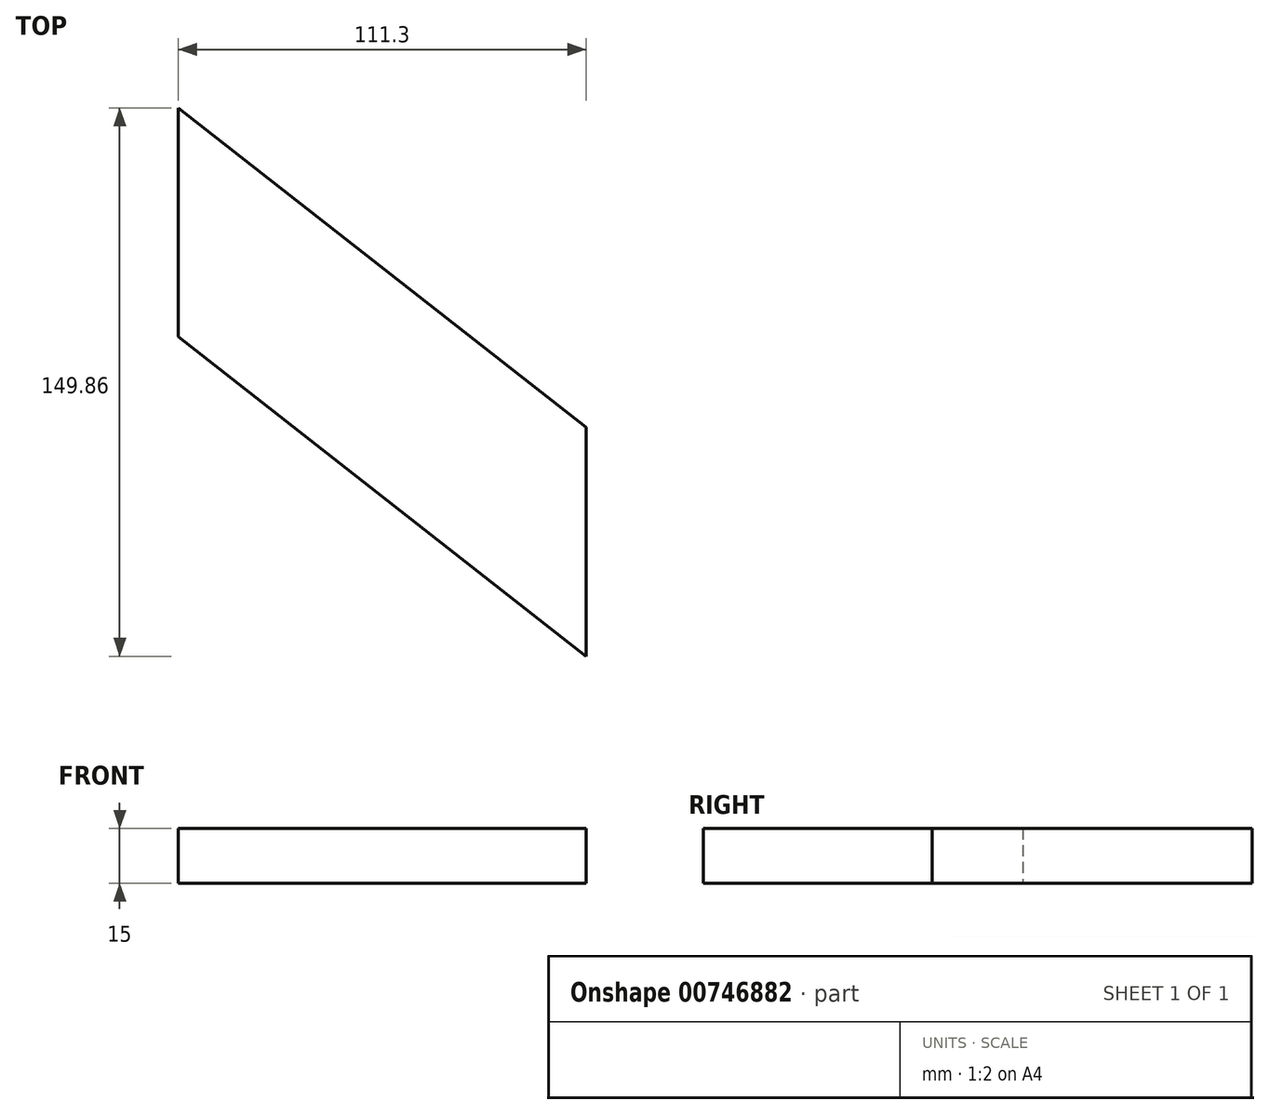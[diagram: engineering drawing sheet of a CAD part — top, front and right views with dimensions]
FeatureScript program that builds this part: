
annotation { "Feature Type Name" : "Feature", "Feature Type Description" : "" }
export const myFeature = defineFeature(function(context is Context, id is Id, definition is map)
    precondition{}
    {
        {
            var Q0;
            Q0=qCreatedBy(makeId("Top.planeOp"),FACE);
            var sketch = newSketch(context, id + "F0", { "sketchPlane" : qUnion([Q0])});
            skLineSegment(sketch, "E0", {"start": v(0, 0) * mm, "end": v(111.3, 87.3) * mm});
            skLineSegment(sketch, "E1", {"start": v(111.3, 87.3) * mm, "end": v(111.3, 149.86) * mm});
            skLineSegment(sketch, "E2", {"start": v(111.3, 149.86) * mm, "end": v(0, 62.56) * mm});
            skLineSegment(sketch, "E3", {"start": v(0, 62.56) * mm, "end": v(0, 0) * mm});
            skLineSegment(sketch, "E4.MirrorCS", {"start": v(0, 0) * mm, "end": v(-111.3, 87.3) * mm});
            skLineSegment(sketch, "E5.MirrorCS", {"start": v(-111.3, 87.3) * mm, "end": v(-111.3, 149.86) * mm});
            skLineSegment(sketch, "E6.MirrorCS", {"start": v(-111.3, 149.86) * mm, "end": v(0, 62.56) * mm});
            skSolve(sketch);
        }
        {
            var Q0;
            Q0=makeQuery(id+"F0.imprint","IMPRINT",FACE,{"disambiguationData":[TD([[makeQuery(id+"F0.imprint","IMPRINT",EDGE,{"derivedFrom":sQuery(id+"F0.wireOp",EDGE,"E0")}),1.0]])]});
            var sketch = newSketch(context, id + "F1", { "sketchPlane" : qUnion([Q0])});
            skSolve(sketch);
        }
        {
            var Q0;
            Q0=makeQuery(id+"F0.imprint","IMPRINT",FACE,{"disambiguationData":[TD([[makeQuery(id+"F0.imprint","IMPRINT",EDGE,{"derivedFrom":sQuery(id+"F0.wireOp",EDGE,"E3")}),-1.0]])]});
            var Q1;
            Q1=makeQuery(id+"F1.imprint","IMPRINT",FACE,{"disambiguationData":[TD([[makeQuery(id+"F1.imprint","IMPRINT",EDGE,{"derivedFrom":makeQuery(id+"F0.imprint","IMPRINT",EDGE,{"derivedFrom":sQuery(id+"F0.wireOp",EDGE,"E0")})}),1.0]])]});
            extrude(context, id + "F2", {"entities" : qUnion([Q0, Q1]), "depth" : 15 * mm, "offsetDistance" : 25 * mm});
        }
    });
